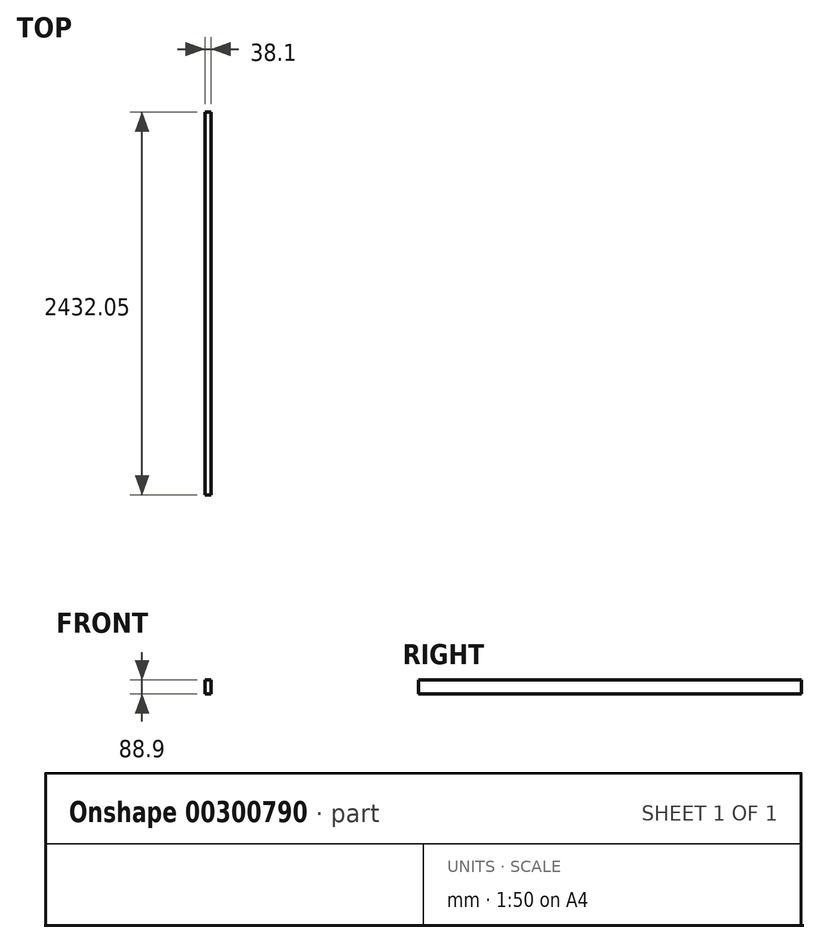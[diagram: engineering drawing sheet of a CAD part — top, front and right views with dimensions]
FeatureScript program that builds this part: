
annotation { "Feature Type Name" : "Feature", "Feature Type Description" : "" }
export const myFeature = defineFeature(function(context is Context, id is Id, definition is map)
    precondition{}
    {
        {
            var Q0;
            Q0=qCreatedBy(makeId("Front.planeOp"),FACE);
            var sketch = newSketch(context, id + "F0", { "sketchPlane" : qUnion([Q0])});
            skLineSegment(sketch, "E0.bottom", {"start": v(0, 0) * mm, "end": v(38.1, 0) * mm});
            skLineSegment(sketch, "E0.top", {"start": v(0, 88.9) * mm, "end": v(38.1, 88.9) * mm});
            skLineSegment(sketch, "E0.left", {"start": v(0, 0) * mm, "end": v(0, 88.9) * mm});
            skLineSegment(sketch, "E0.right", {"start": v(38.1, 0) * mm, "end": v(38.1, 88.9) * mm});
            skSolve(sketch);
        }
        {
            var Q0;
            Q0 = qSketchRegion(id + "F0", true);
            extrude(context, id + "F1", {"entities" : qUnion([Q0]), "oppositeDirection" : true, "depth" : 2432.05 * mm});
        }
    });
